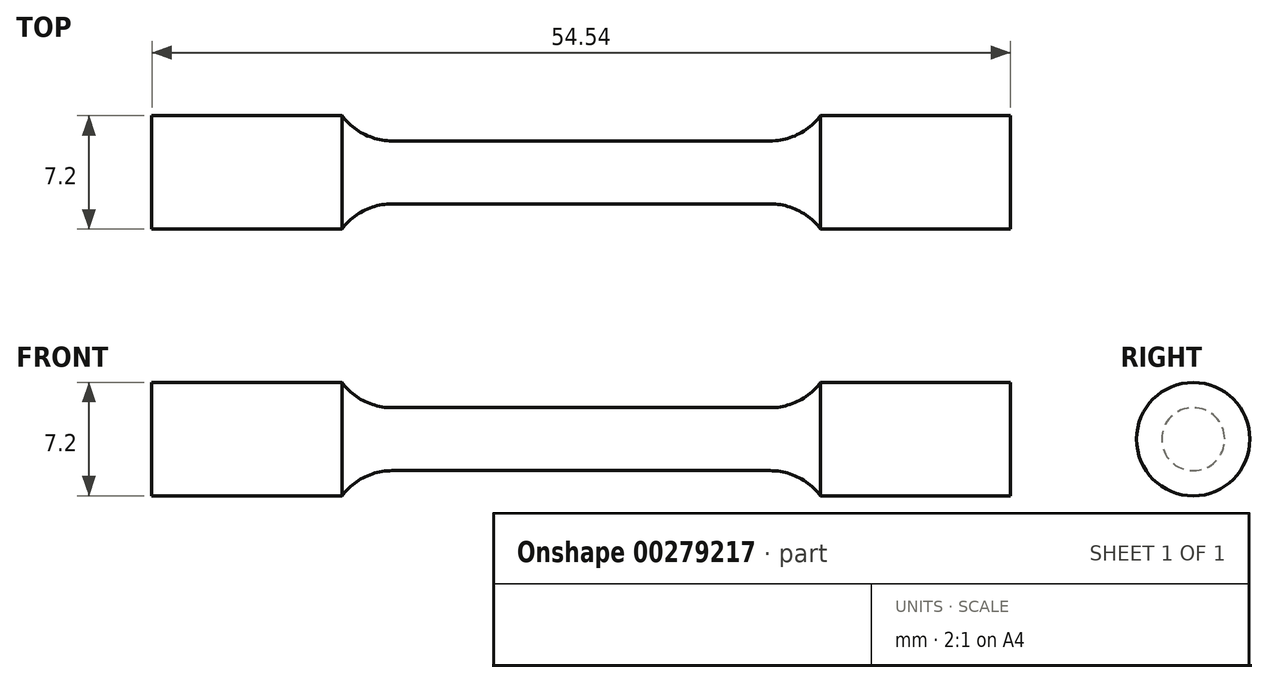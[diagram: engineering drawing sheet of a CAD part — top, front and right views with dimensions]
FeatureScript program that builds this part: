
annotation { "Feature Type Name" : "Feature", "Feature Type Description" : "" }
export const myFeature = defineFeature(function(context is Context, id is Id, definition is map)
    precondition{}
    {
        {
            var Q0;
            Q0=qCreatedBy(makeId("Front.planeOp"),FACE);
            var sketch = newSketch(context, id + "F0", { "sketchPlane" : qUnion([Q0])});
            skLineSegment(sketch, "E0", {"start": v(0, 2) * mm, "end": v(12, 2) * mm});
            skArc(sketch, "E1", {"start": v(12, 2) * mm, "mid": v(13.79, 2.42) * mm, "end": v(15.2, 3.6) * mm});
            skLineSegment(sketch, "E2", {"start": v(15.2, 3.6) * mm, "end": v(27.27, 3.6) * mm});
            skLineSegment(sketch, "E3", {"start": v(27.27, 3.6) * mm, "end": v(27.27, 0) * mm});
            skLineSegment(sketch, "E4.MirrorCS", {"start": v(0, 2) * mm, "end": v(-12, 2) * mm});
            skArc(sketch, "E5.MirrorCS", {"start": v(-12, 2) * mm, "mid": v(-13.79, 2.42) * mm, "end": v(-15.2, 3.6) * mm});
            skLineSegment(sketch, "E6.MirrorCS", {"start": v(-27.27, 3.6) * mm, "end": v(-27.27, 0) * mm});
            skLineSegment(sketch, "E7.MirrorCS", {"start": v(-15.2, 3.6) * mm, "end": v(-27.27, 3.6) * mm});
            skLineSegment(sketch, "E8", {"start": v(-27.27, 0) * mm, "end": v(27.27, 0) * mm});
            skSolve(sketch);
        }
        {
            var Q0;
            Q0 = qSketchRegion(id + "F0", true);
            var Q1;
            Q1=sQuery(id+"F0.wireOp",EDGE,"E8");
            revolve(context, id + "F1", {"entities" : qUnion([Q0]), "axis" : qUnion([Q1]), "revolveType" : RevolveType.FULL});
        }
    });
